# Revit family: QF_Vollrath_912HIDC
name_source: partatom
category: Specialty Equipment
revit_build: Autodesk Revit 2016 (Build: 20151007_0715(x64)
units: mm (PartAtom-declared; Revit-internal decimal feet)

## family parameters
Always vertical = Yes
Cut with Voids When Loaded = No
OmniClass Number = 23.40.40.11.21
OmniClass Title = Hot Cabinets
Part Type = Normal
Room Calculation Point = No
Round Connector Dimension = Use Diameter
Shared = No
Work Plane-Based = No

## types (2) — shared parameters
Assembly Code = E1090320
CSI MasterFormat = 11 42 13
Conn Plug = NEMA 6-30P
Cycle = 60 Hz
Description = Induction Hot Plate
FL Amps = 24 A
Manufacturer = Vollrath
Model = 912HIDC
Phase = 1
URL = www.vollrathco.com

## per-type parameters (varying)
| type | Apparent Power | Elec Conn Connection Height | Volts | Watts | Weight in Pounds |
| 208V | 4992 VA | 6 " | 208 V | 5000 W | 60.25 |
| 240V | 5760 VA | 2 " | 240 V | 5800 W | 47 |

## geometry (parser evidence)
native form markers: Blend x14, Sweep x2
no freeform markers — native parametric forms only
